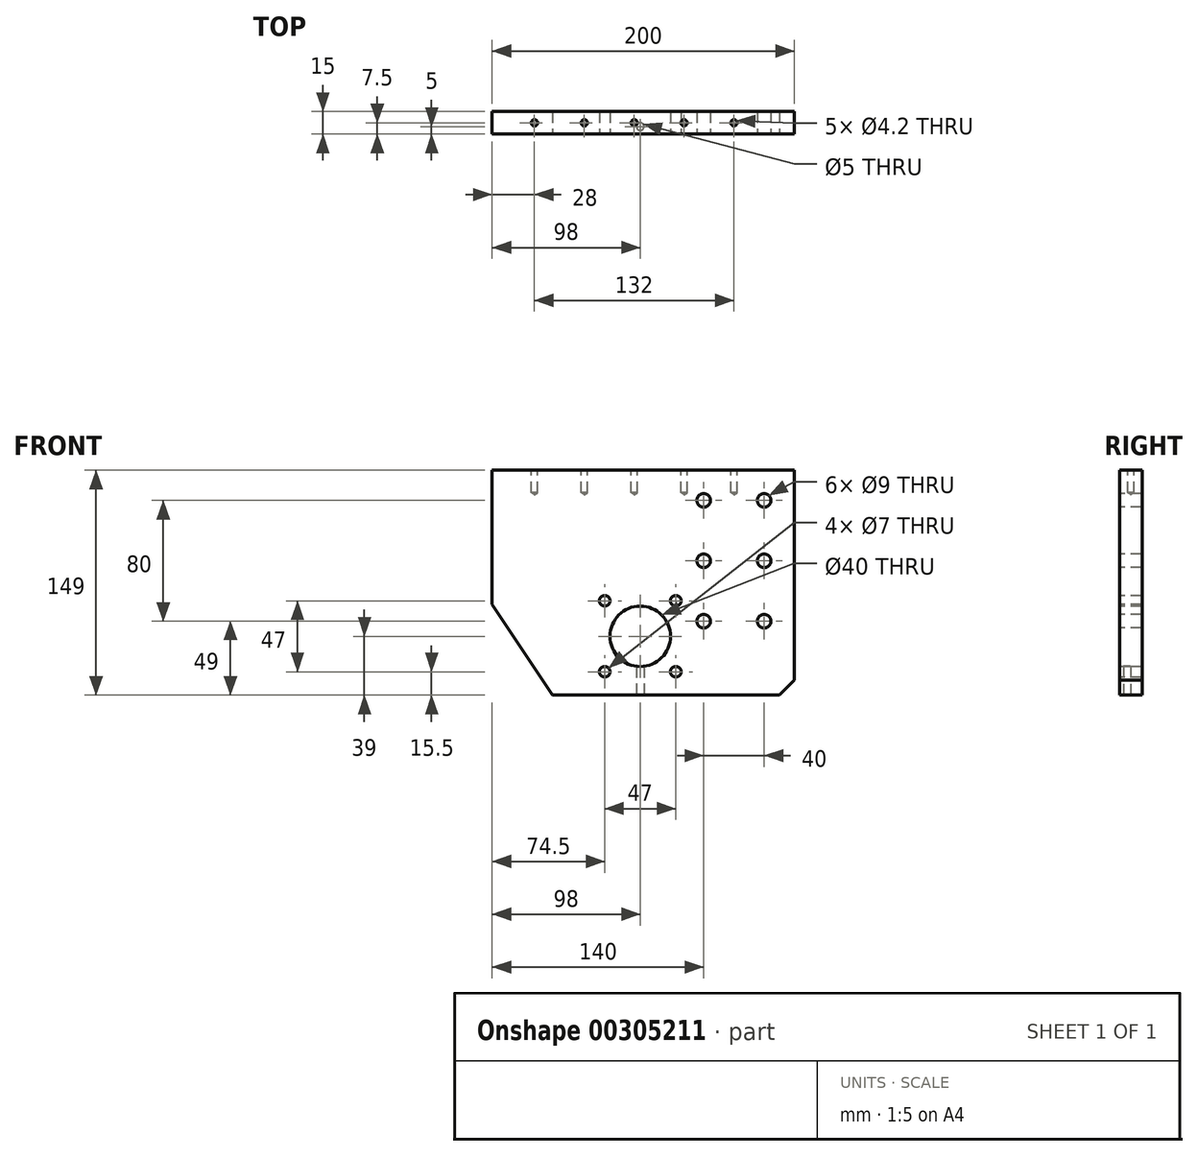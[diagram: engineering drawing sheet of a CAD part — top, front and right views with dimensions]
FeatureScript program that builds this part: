
annotation { "Feature Type Name" : "Feature", "Feature Type Description" : "" }
export const myFeature = defineFeature(function(context is Context, id is Id, definition is map)
    precondition{}
    {
        {
            var Q0;
            Q0=qCreatedBy(makeId("Front.planeOp"),FACE);
            var sketch = newSketch(context, id + "F0", { "sketchPlane" : qUnion([Q0])});
            skLineSegment(sketch, "E0.bottom", {"start": v(0, 0) * mm, "end": v(200, 0) * mm});
            skLineSegment(sketch, "E0.top", {"start": v(0, 200) * mm, "end": v(200, 200) * mm});
            skLineSegment(sketch, "E0.left", {"start": v(0, 0) * mm, "end": v(0, 200) * mm});
            skLineSegment(sketch, "E0.right", {"start": v(200, 0) * mm, "end": v(200, 200) * mm});
            skSolve(sketch);
        }
        {
            var Q0;
            Q0=makeQuery(id+"F0.imprint","IMPRINT",FACE,{"disambiguationData":[TD([[makeQuery(id+"F0.imprint","IMPRINT",EDGE,{"derivedFrom":sQuery(id+"F0.wireOp",EDGE,"E0.bottom")}),1.0]])]});
            extrude(context, id + "F1", {"entities" : qUnion([Q0]), "depth" : 15 * mm});
        }
        {
            var Q0;
            Q0=makeQuery(id+"F1.opExtrude","CAP_FACE",FACE,{"disambiguationData":[OSD([sQuery(id+"F0.wireOp",EDGE,"E0.bottom"),sQuery(id+"F0.wireOp",EDGE,"E0.top"),sQuery(id+"F0.wireOp",EDGE,"E0.left"),sQuery(id+"F0.wireOp",EDGE,"E0.right")])],"isStart":false});
            var sketch = newSketch(context, id + "F2", { "sketchPlane" : qUnion([Q0])});
            skCircle(sketch, "E1", {"center": v(98, 90) * mm, "radius": 20 * mm});
            skSolve(sketch);
        }
        {
            var Q0;
            Q0=makeQuery(id+"F2.imprint","IMPRINT",FACE,{"disambiguationData":[TD([[makeQuery(id+"F2.imprint","IMPRINT",EDGE,{"derivedFrom":sQuery(id+"F2.wireOp",EDGE,"E1")}),1.0]])]});
            extrude(context, id + "F3", {"entities" : qUnion([Q0]), "operationType" : NewBodyOperationType.REMOVE, "oppositeDirection" : true, "depth" : 25 * mm});
        }
        {
            var Q0;
            Q0=makeQuery(id+"F1.opExtrude","SWEPT_FACE",FACE,{"disambiguationData":[OSD([sQuery(id+"F0.wireOp",EDGE,"E0.bottom")])]});
            extrude(context, id + "F4", {"entities" : qUnion([Q0]), "operationType" : NewBodyOperationType.REMOVE, "oppositeDirection" : true, "depth" : 25 * mm});
        }
        {
            var Q0;
            Q0=makeQuery(id+"F4.boolean.opBoolean","COPY",FACE,{"derivedFrom":makeQuery(id+"F4.opExtrude","CAP_FACE",FACE,{"disambiguationData":[OSD([sQuery(id+"F0.wireOp",EDGE,"E0.bottom")])],"isStart":false})});
            extrude(context, id + "F5", {"entities" : qUnion([Q0]), "operationType" : NewBodyOperationType.REMOVE, "oppositeDirection" : true, "depth" : 26 * mm});
        }
        {
            var Q0;
            Q0=makeQuery(id+"F1.opExtrude","SWEPT_FACE",FACE,{"disambiguationData":[OSD([sQuery(id+"F0.wireOp",EDGE,"E0.left")])]});
            extrude(context, id + "F6", {"entities" : qUnion([Q0]), "operationType" : NewBodyOperationType.REMOVE, "oppositeDirection" : true, "depth" : 30 * mm});
        }
        {
            var Q0;
            Q0=makeQuery(id+"F6.boolean.opBoolean","COPY",FACE,{"derivedFrom":makeQuery(id+"F6.opExtrude","CAP_FACE",FACE,{"disambiguationData":[OSD([sQuery(id+"F0.wireOp",EDGE,"E0.left")])],"isStart":false})});
            extrude(context, id + "F7", {"entities" : qUnion([Q0]), "operationType" : NewBodyOperationType.REMOVE, "oppositeDirection" : true, "depth" : 29 * mm});
        }
        {
            var Q0;
            Q0=makeQuery(id+"F1.opExtrude","CAP_FACE",FACE,{"disambiguationData":[OSD([sQuery(id+"F0.wireOp",EDGE,"E0.bottom"),sQuery(id+"F0.wireOp",EDGE,"E0.top"),sQuery(id+"F0.wireOp",EDGE,"E0.left"),sQuery(id+"F0.wireOp",EDGE,"E0.right")])],"isStart":false});
            var sketch = newSketch(context, id + "F8", { "sketchPlane" : qUnion([Q0])});
            skLineSegment(sketch, "E2", {"start": v(200, 61) * mm, "end": v(190, 51) * mm});
            skSolve(sketch);
        }
        {
            var Q0;
            {var subQ0=sQuery(id+"F8.wireOp",EDGE,"E2");Q0=makeQuery(id+"F8.imprint","IMPRINT",FACE,{"disambiguationData":[TD([[makeQuery(id+"F8.imprint","IMPRINT",EDGE,{"derivedFrom":subQ0}),1.0]])]});}
            extrude(context, id + "F9", {"entities" : qUnion([Q0]), "operationType" : NewBodyOperationType.REMOVE, "oppositeDirection" : true, "depth" : 25 * mm});
        }
        {
            var Q0;
            Q0=makeQuery(id+"F2.imprint","IMPRINT",FACE,{"disambiguationData":[TD([[makeQuery(id+"F2.imprint","IMPRINT",EDGE,{"derivedFrom":sQuery(id+"F2.wireOp",EDGE,"E1")}),-1.0]])]});
            var sketch = newSketch(context, id + "F10", { "sketchPlane" : qUnion([Q0])});
            skCircle(sketch, "E3", {"center": v(180, 100) * mm, "radius": 4.5 * mm});
            skPoint(sketch, "E4", {"position": v(140, 100) * mm});
            skPoint(sketch, "E5", {"position": v(140, 140) * mm});
            skPoint(sketch, "E6", {"position": v(180, 140) * mm});
            skPoint(sketch, "E7", {"position": v(180, 180) * mm});
            skPoint(sketch, "E8", {"position": v(140, 180) * mm});
            skPoint(sketch, "E9", {"position": v(74.5, 66.5) * mm});
            skPoint(sketch, "E10", {"position": v(74.5, 113.5) * mm});
            skPoint(sketch, "E11", {"position": v(121.5, 113.5) * mm});
            skPoint(sketch, "E12", {"position": v(121.5, 66.5) * mm});
            skSolve(sketch);
        }
        {
            var Q0;
            Q0=sQuery(id+"F10.wireOp",VERTEX,"E3.center");
            var Q1;
            Q1=sQuery(id+"F10.wireOp",VERTEX,"E6");
            var Q2;
            Q2=sQuery(id+"F10.wireOp",VERTEX,"E7");
            var Q3;
            Q3=sQuery(id+"F10.wireOp",VERTEX,"E8");
            var Q4;
            Q4=sQuery(id+"F10.wireOp",VERTEX,"E5");
            var Q5;
            Q5=sQuery(id+"F10.wireOp",VERTEX,"E4");
            var Q6;
            Q6=makeQuery(id+"F1.opExtrude","SWEPT_BODY",BODY,{"disambiguationData":[OSD([sQuery(id+"F0.wireOp",EDGE,"E0.bottom"),sQuery(id+"F0.wireOp",EDGE,"E0.top"),sQuery(id+"F0.wireOp",EDGE,"E0.left"),sQuery(id+"F0.wireOp",EDGE,"E0.right")])]});
            hole(context, id + "F11", {"style" : HoleStyle.SIMPLE, "endStyle" : HoleEndStyle.THROUGH, "holeDiameter" : 9 * mm, "tappedDepth" : 12.6 * mm, "tapClearance" : 3, "startFromSketch" : true, "locations" : qUnion([Q0, Q1, Q2, Q3, Q4, Q5]), "scope" : qUnion([Q6])});
        }
        {
            var Q0;
            Q0=sQuery(id+"F10.wireOp",VERTEX,"E12");
            var Q1;
            Q1=sQuery(id+"F10.wireOp",VERTEX,"E11");
            var Q2;
            Q2=sQuery(id+"F10.wireOp",VERTEX,"E9");
            var Q3;
            Q3=sQuery(id+"F10.wireOp",VERTEX,"E10");
            var Q4;
            Q4=makeQuery(id+"F1.opExtrude","SWEPT_BODY",BODY,{"disambiguationData":[OSD([sQuery(id+"F0.wireOp",EDGE,"E0.bottom"),sQuery(id+"F0.wireOp",EDGE,"E0.top"),sQuery(id+"F0.wireOp",EDGE,"E0.left"),sQuery(id+"F0.wireOp",EDGE,"E0.right")])]});
            hole(context, id + "F12", {"style" : HoleStyle.SIMPLE, "endStyle" : HoleEndStyle.THROUGH, "holeDiameter" : 7 * mm, "tappedDepth" : 12.6 * mm, "tapClearance" : 3, "startFromSketch" : true, "locations" : qUnion([Q0, Q1, Q2, Q3]), "scope" : qUnion([Q4])});
        }
        {
            var Q0;
            Q0=makeQuery(id+"F5.boolean.opBoolean","COPY",FACE,{"derivedFrom":makeQuery(id+"F5.opExtrude","CAP_FACE",FACE,{"disambiguationData":[OSD([sQuery(id+"F0.wireOp",EDGE,"E0.bottom")])],"isStart":false})});
            var sketch = newSketch(context, id + "F13", { "sketchPlane" : qUnion([Q0])});
            skCircle(sketch, "E13", {"center": v(98, 10) * mm, "radius": 2.5 * mm});
            skPoint(sketch, "E13.centerSnap0", {"position": v(59, 10) * mm});
            skSolve(sketch);
        }
        {
            var Q0;
            Q0=sQuery(id+"F13.wireOp",VERTEX,"E13.center");
            var Q1;
            Q1=makeQuery(id+"F1.opExtrude","SWEPT_BODY",BODY,{"disambiguationData":[OSD([sQuery(id+"F0.wireOp",EDGE,"E0.bottom"),sQuery(id+"F0.wireOp",EDGE,"E0.top"),sQuery(id+"F0.wireOp",EDGE,"E0.left"),sQuery(id+"F0.wireOp",EDGE,"E0.right")])]});
            hole(context, id + "F14", {"style" : HoleStyle.SIMPLE, "endStyle" : HoleEndStyle.BLIND, "holeDiameter" : 5 * mm, "holeDepth" : 20 * mm, "tappedDepth" : 12 * mm, "tapClearance" : 3, "startFromSketch" : true, "locations" : qUnion([Q0]), "scope" : qUnion([Q1])});
        }
        {
            var Q0;
            Q0=makeQuery(id+"F7.boolean.opBoolean","COPY",FACE,{"derivedFrom":makeQuery(id+"F7.opExtrude","CAP_FACE",FACE,{"disambiguationData":[OSD([sQuery(id+"F0.wireOp",EDGE,"E0.left")])],"isStart":false})});
            extrude(context, id + "F15", {"entities" : qUnion([Q0]), "operationType" : NewBodyOperationType.ADD, "depth" : 4 * mm});
        }
        {
            var Q0;
            Q0=makeQuery(id+"F15.opExtrude","CAP_FACE",FACE,{"disambiguationData":[OSD([sQuery(id+"F0.wireOp",EDGE,"E0.left")])],"isStart":false});
            extrude(context, id + "F16", {"entities" : qUnion([Q0]), "operationType" : NewBodyOperationType.ADD, "depth" : 55 * mm});
        }
        {
            var Q0;
            Q0=makeQuery(id+"F2.imprint","IMPRINT",FACE,{"disambiguationData":[TD([[makeQuery(id+"F2.imprint","IMPRINT",EDGE,{"derivedFrom":sQuery(id+"F2.wireOp",EDGE,"E1")}),-1.0]])]});
            var sketch = newSketch(context, id + "F17", { "sketchPlane" : qUnion([Q0])});
            skLineSegment(sketch, "E14.0", {"start": v(0, 51) * mm, "end": v(190, 51) * mm});
            skLineSegment(sketch, "E15.0", {"start": v(0, 51) * mm, "end": v(0, 200) * mm});
            skPoint(sketch, "E16", {"position": v(40, 51) * mm});
            skPoint(sketch, "E17", {"position": v(0, 111) * mm});
            skLineSegment(sketch, "E18", {"start": v(40, 51) * mm, "end": v(0, 111) * mm});
            skSolve(sketch);
        }
        {
            var Q0;
            {var subQ3=sQuery(id+"F17.wireOp",EDGE,"E18");Q0=makeQuery(id+"F17.imprint","IMPRINT",FACE,{"disambiguationData":[TD([[makeQuery(id+"F17.imprint","IMPRINT",EDGE,{"derivedFrom":subQ3}),1.0]])]});}
            extrude(context, id + "F18", {"entities" : qUnion([Q0]), "operationType" : NewBodyOperationType.REMOVE, "oppositeDirection" : true, "depth" : 25 * mm});
        }
        {
            var Q0;
            {var subQ0=sQuery(id+"F0.wireOp",EDGE,"E0.left");var subQ1=sQuery(id+"F0.wireOp",EDGE,"E0.top");Q0=makeQuery(id+"F16.boolean.opBoolean","MERGE",FACE,{"derivedFrom":[makeQuery(id+"F15.boolean.opBoolean","MERGE",FACE,{"derivedFrom":[makeQuery(id+"F1.opExtrude","SWEPT_FACE",FACE,{"disambiguationData":[OSD([subQ1])]}),makeQuery(id+"F15.opExtrude","SWEPT_FACE",FACE,{"disambiguationData":[OSD([subQ1,subQ0])]})]}),makeQuery(id+"F16.opExtrude","SWEPT_FACE",FACE,{"disambiguationData":[OSD([subQ1,subQ0])]})]});}
            var sketch = newSketch(context, id + "F19", { "sketchPlane" : qUnion([Q0])});
            skPoint(sketch, "E19", {"position": v(160, -7.5) * mm});
            skPoint(sketch, "E20", {"position": v(127, -7.5) * mm});
            skPoint(sketch, "E21", {"position": v(94, -7.5) * mm});
            skPoint(sketch, "E22", {"position": v(28, -7.5) * mm});
            skPoint(sketch, "E23", {"position": v(61, -7.5) * mm});
            skSolve(sketch);
        }
        {
            var Q0;
            Q0=sQuery(id+"F19.wireOp",VERTEX,"E22");
            var Q1;
            Q1=sQuery(id+"F19.wireOp",VERTEX,"E23");
            var Q2;
            Q2=sQuery(id+"F19.wireOp",VERTEX,"E21");
            var Q3;
            Q3=sQuery(id+"F19.wireOp",VERTEX,"E20");
            var Q4;
            Q4=sQuery(id+"F19.wireOp",VERTEX,"E19");
            var Q5;
            Q5=makeQuery(id+"F1.opExtrude","SWEPT_BODY",BODY,{"disambiguationData":[OSD([sQuery(id+"F0.wireOp",EDGE,"E0.bottom"),sQuery(id+"F0.wireOp",EDGE,"E0.top"),sQuery(id+"F0.wireOp",EDGE,"E0.left"),sQuery(id+"F0.wireOp",EDGE,"E0.right")])]});
            hole(context, id + "F20", {"style" : HoleStyle.SIMPLE, "endStyle" : HoleEndStyle.BLIND, "standardTappedOrClearance" : lookupTablePath({ "standard" : "ISO", "engagement" : "75%", "pitch" : "0.8 mm", "size" : "M5", "type" : "Tapped" }), "standardBlindInLast" : lookupTablePath({ "standard" : "ISO", "engagement" : "75%", "pitch" : "0.8 mm", "size" : "M5", "type" : "Tapped" }), "holeDiameter" : 4.2 * mm, "showTappedDepth" : true, "holeDepth" : 15 * mm, "tappedDepth" : 12.6 * mm, "tapClearance" : 3, "startFromSketch" : true, "locations" : qUnion([Q0, Q1, Q2, Q3, Q4]), "scope" : qUnion([Q5]), "majorDiameter" : 5 * mm});
        }
    });
